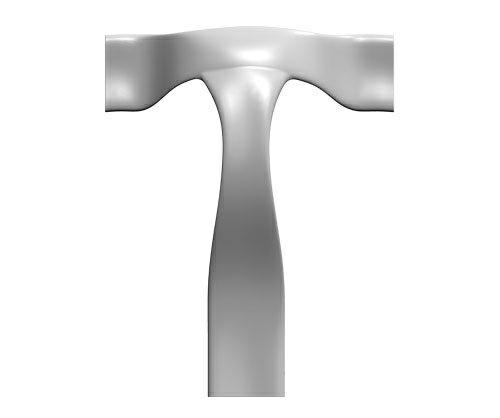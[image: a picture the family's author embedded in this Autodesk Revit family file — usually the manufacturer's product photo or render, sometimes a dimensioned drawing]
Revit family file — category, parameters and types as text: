
# Revit family: CITY ALPHABET letter „T”
name_source: partatom
category: Furniture
revit_build: Autodesk Revit 2018 (Build: 20190510_1515(x64)
units: mm (PartAtom-declared; Revit-internal decimal feet)

## family parameters
Cut with Voids When Loaded = No
Host = Face
OmniClass Number = 23.40.10.11.14
OmniClass Title = Exterior Seating
Room Calculation Point = No
Shared = No

## types (1)
- CITY ALPHABET letter „T”
    Default Elevation = 1219 mm
    Height = 710 mm
    IfcExportAs = IfcFurnishingElement
    Length = 2310 mm  [stored 7.57874 ft]
    Manufacturer = Astrini Design
    Material information = Colour choice from RAL colour standard. Customer may inquire about specific request regarding individual order.
    Model = CITY ALPHABET letter „T”
    Operating temperature = -40°C to 80°C, ( -40°F to 176°F )
    Type Comments = Bench
    Type Image = T.jpg
    URL = https://astrini-design.pl
    Weight (approximately) = 41.00 kg
    Weight - filled (approximately) = 91.00 kg
    Width = 1800 mm  [stored 5.90551 ft]

note: [stored X ft] marks values corroborated as IEEE doubles in the binary element streams (Revit-internal decimal feet)
